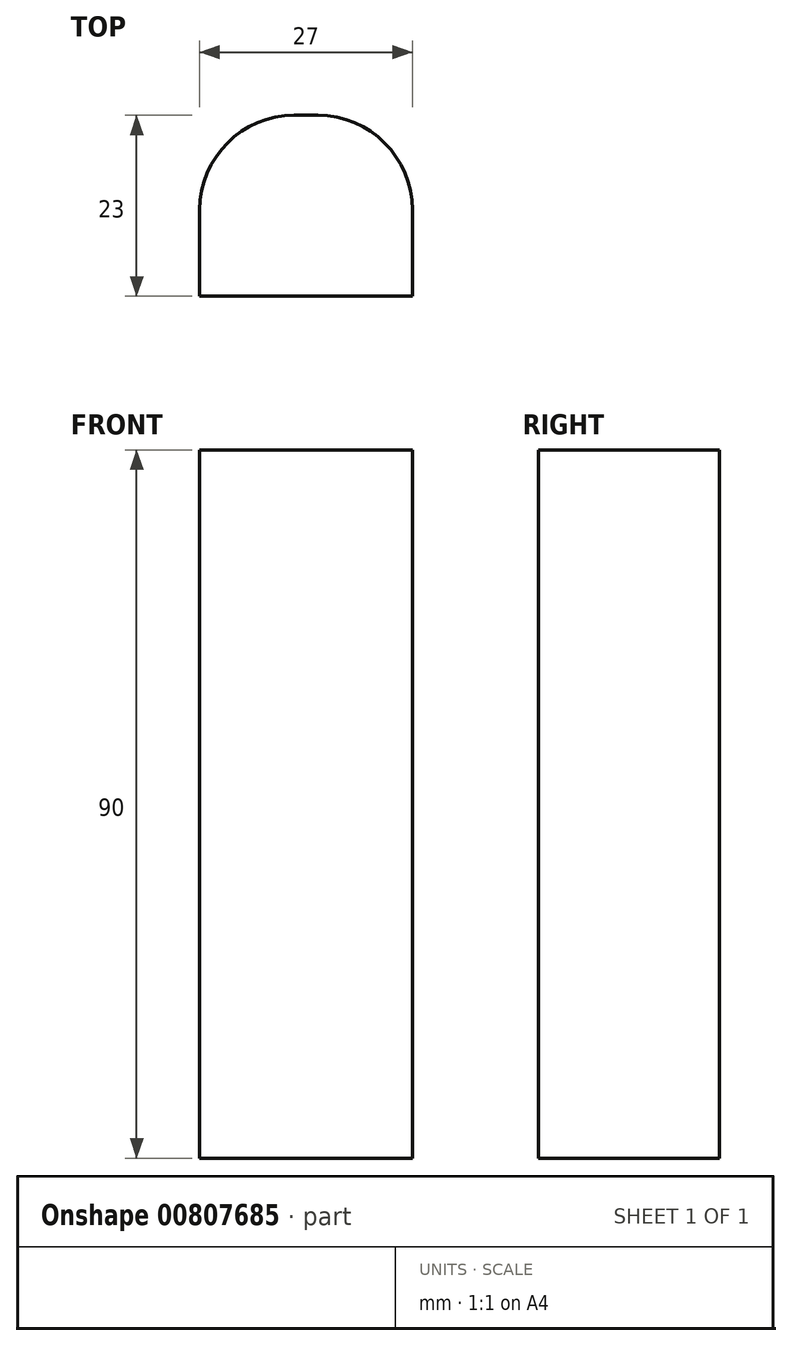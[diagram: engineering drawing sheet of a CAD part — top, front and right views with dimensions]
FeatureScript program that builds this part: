
annotation { "Feature Type Name" : "Feature", "Feature Type Description" : "" }
export const myFeature = defineFeature(function(context is Context, id is Id, definition is map)
    precondition{}
    {
        {
            var Q0;
            Q0=qCreatedBy(makeId("Top.planeOp"),FACE);
            var sketch = newSketch(context, id + "F0", { "sketchPlane" : qUnion([Q0])});
            skLineSegment(sketch, "E0.bottom", {"start": v(-67.21, 0) * mm, "end": v(-50.21, 0) * mm});
            skLineSegment(sketch, "E0.top", {"start": v(14, 23) * mm, "end": v(17, 23) * mm});
            skLineSegment(sketch, "E0.left", {"start": v(2, 0) * mm, "end": v(2, 11) * mm});
            skLineSegment(sketch, "E0.right", {"start": v(29, 0) * mm, "end": v(29, 11) * mm});
            skPoint(sketch, "E1.visualSharp", {"position": v(2, 23) * mm});
            skArc(sketch, "E1.filletArc", {"start": v(14, 23) * mm, "mid": v(5.51, 19.49) * mm, "end": v(2, 11) * mm});
            skPoint(sketch, "E2.visualSharp", {"position": v(29, 23) * mm});
            skArc(sketch, "E2.filletArc", {"start": v(29, 11) * mm, "mid": v(25.49, 19.49) * mm, "end": v(17, 23) * mm});
            skPoint(sketch, "E3.visualSharp", {"position": v(29, 0) * mm});
            skPoint(sketch, "E4.visualSharp", {"position": v(2, 0) * mm});
            skLineSegment(sketch, "E5.2", {"start": v(0, 0) * mm, "end": v(0, 11) * mm});
            skArc(sketch, "E5.4", {"start": v(14, 25) * mm, "mid": v(4.1, 20.9) * mm, "end": v(0, 11) * mm});
            skLineSegment(sketch, "E5.5", {"start": v(14, 25) * mm, "end": v(17, 25) * mm});
            skArc(sketch, "E5.6", {"start": v(31, 11) * mm, "mid": v(26.9, 20.9) * mm, "end": v(17, 25) * mm});
            skLineSegment(sketch, "E6", {"start": v(2, 0) * mm, "end": v(0, 0) * mm});
            skLineSegment(sketch, "E7", {"start": v(29, 0) * mm, "end": v(31, 0) * mm});
            skPoint(sketch, "E8.orphan", {"position": v(31, -61.83) * mm});
            skLineSegment(sketch, "E9", {"start": v(31, 11) * mm, "end": v(31, 0) * mm});
            skLineSegment(sketch, "E10", {"start": v(2, 0) * mm, "end": v(29, 0) * mm});
            skSolve(sketch);
        }
        {
            var Q0;
            Q0=makeQuery(id+"F0.imprint","IMPRINT",FACE,{"disambiguationData":[TD([[makeQuery(id+"F0.imprint","IMPRINT",EDGE,{"derivedFrom":sQuery(id+"F0.wireOp",EDGE,"E0.top")}),-1.0]])]});
            extrude(context, id + "F1", {"entities" : qUnion([Q0]), "depth" : 90 * mm, "offsetDistance" : 25 * mm});
        }
    });
